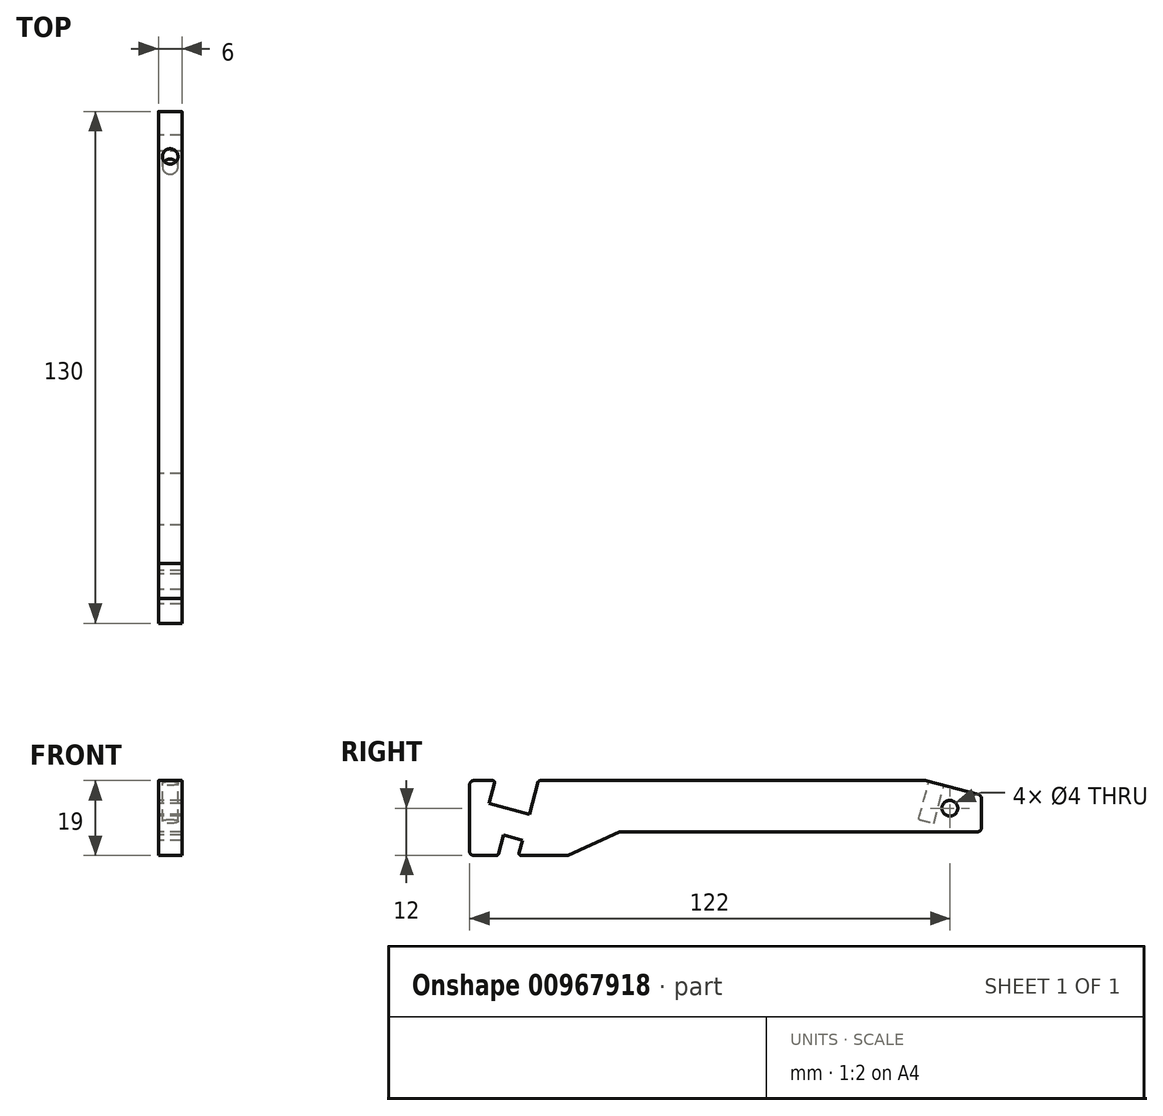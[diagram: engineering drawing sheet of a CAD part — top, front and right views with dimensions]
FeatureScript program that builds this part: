
annotation { "Feature Type Name" : "Feature", "Feature Type Description" : "" }
export const myFeature = defineFeature(function(context is Context, id is Id, definition is map)
    precondition{}
    {
        {
            var Q0;
            Q0=qCreatedBy(makeId("Right.planeOp"),FACE);
            var sketch = newSketch(context, id + "F0", { "sketchPlane" : qUnion([Q0])});
            skLineSegment(sketch, "E0.bottom", {"start": v(-1, 0) * mm, "end": v(-92, 0) * mm});
            skLineSegment(sketch, "E0.top", {"start": v(-14.13, 13) * mm, "end": v(-92, 13) * mm});
            skLineSegment(sketch, "E0.left", {"start": v(0, 1) * mm, "end": v(0, 8.48) * mm});
            skLineSegment(sketch, "E1", {"start": v(-13.87, 12.97) * mm, "end": v(-0.74, 9.45) * mm});
            skCircle(sketch, "E2", {"center": v(-8, 6) * mm, "radius": 2 * mm});
            skLineSegment(sketch, "E3.bottom", {"start": v(-105, 13) * mm, "end": v(-112.12, 13) * mm});
            skLineSegment(sketch, "E3.top", {"start": v(-105, -6) * mm, "end": v(-116.94, -6) * mm});
            skLineSegment(sketch, "E3.right", {"start": v(-130, 12) * mm, "end": v(-130, -5) * mm});
            skLineSegment(sketch, "E4", {"start": v(-92, 0) * mm, "end": v(-105, -6) * mm});
            skLineSegment(sketch, "E5", {"start": v(-92, 13) * mm, "end": v(-105, 13) * mm});
            skLineSegment(sketch, "E6", {"start": v(-112.6, 12.63) * mm, "end": v(-114.8, 4.45) * mm});
            skLineSegment(sketch, "E7", {"start": v(-116.56, -2.14) * mm, "end": v(-117.42, -5.37) * mm});
            skPoint(sketch, "E7.endSnap0", {"position": v(-117.5, -6) * mm});
            skLineSegment(sketch, "E8", {"start": v(-125.06, 7.2) * mm, "end": v(-123.67, 12.37) * mm});
            skLineSegment(sketch, "E9", {"start": v(-121.39, -0.84) * mm, "end": v(-122.67, -5.63) * mm});
            skPoint(sketch, "E10.start.orphan", {"position": v(-114.53, 5.43) * mm});
            skLineSegment(sketch, "E11", {"start": v(-125.06, 7.2) * mm, "end": v(-114.8, 4.45) * mm});
            skLineSegment(sketch, "E12", {"start": v(-121.39, -0.84) * mm, "end": v(-116.56, -2.14) * mm});
            skPoint(sketch, "E13.visualSharp", {"position": v(-130, 13) * mm});
            skArc(sketch, "E13.filletArc", {"start": v(-129, 13) * mm, "mid": v(-129.7, 12.7) * mm, "end": v(-130, 12) * mm});
            skPoint(sketch, "E14.visualSharp", {"position": v(-130, -6) * mm});
            skArc(sketch, "E14.filletArc", {"start": v(-130, -5) * mm, "mid": v(-129.7, -5.7) * mm, "end": v(-129, -6) * mm});
            skLineSegment(sketch, "E15.trimOffspring", {"start": v(-124.16, 13) * mm, "end": v(-129, 13) * mm});
            skLineSegment(sketch, "E16.trimOffspring", {"start": v(-123.15, -6) * mm, "end": v(-129, -6) * mm});
            skPoint(sketch, "E17.visualSharp", {"position": v(-123.5, 13) * mm});
            skArc(sketch, "E17.filletArc", {"start": v(-123.67, 12.37) * mm, "mid": v(-123.76, 12.8) * mm, "end": v(-124.16, 13) * mm});
            skPoint(sketch, "E18.visualSharp", {"position": v(-112.5, 13) * mm});
            skArc(sketch, "E18.filletArc", {"start": v(-112.12, 13) * mm, "mid": v(-112.42, 12.9) * mm, "end": v(-112.6, 12.63) * mm});
            skPoint(sketch, "E19.visualSharp", {"position": v(-117.6, -6) * mm});
            skArc(sketch, "E19.filletArc", {"start": v(-117.42, -5.37) * mm, "mid": v(-117.34, -5.8) * mm, "end": v(-116.94, -6) * mm});
            skPoint(sketch, "E20.visualSharp", {"position": v(-122.77, -6) * mm});
            skArc(sketch, "E20.filletArc", {"start": v(-123.15, -6) * mm, "mid": v(-122.85, -5.9) * mm, "end": v(-122.67, -5.63) * mm});
            skPoint(sketch, "E21.visualSharp", {"position": v(-14, 13) * mm});
            skArc(sketch, "E21.filletArc", {"start": v(-13.87, 12.97) * mm, "mid": v(-14, 13) * mm, "end": v(-14.13, 13) * mm});
            skPoint(sketch, "E22.visualSharp", {"position": v(0, 9.25) * mm});
            skArc(sketch, "E22.filletArc", {"start": v(0, 8.48) * mm, "mid": v(-0.2, 9.1) * mm, "end": v(-0.74, 9.45) * mm});
            skPoint(sketch, "E23.visualSharp", {"position": v(0, 0) * mm});
            skArc(sketch, "E23.filletArc", {"start": v(-1, 0) * mm, "mid": v(-0.3, 0.3) * mm, "end": v(0, 1) * mm});
            skSolve(sketch);
        }
        {
            var Q0;
            Q0 = qSketchRegion(id + "F0", true);
            extrude(context, id + "F1", {"entities" : qUnion([Q0]), "depth" : 6 * mm, "offsetDistance" : 25 * mm});
        }
        {
            var Q0;
            Q0=makeQuery(id+"F1.opExtrude","SWEPT_FACE",FACE,{"disambiguationData":[OSD([sQuery(id+"F0.wireOp",EDGE,"E1")])]});
            var sketch = newSketch(context, id + "F2", { "sketchPlane" : qUnion([Q0])});
            skCircle(sketch, "E24", {"center": v(3, -14.2) * mm, "radius": 2 * mm});
            skPoint(sketch, "E24.centerSnap0", {"position": v(3, -16.76) * mm});
            skSolve(sketch);
        }
        {
            var Q0;
            Q0=makeQuery(id+"F2.imprint","IMPRINT",FACE,{"disambiguationData":[TD([[makeQuery(id+"F2.imprint","IMPRINT",EDGE,{"derivedFrom":sQuery(id+"F2.wireOp",EDGE,"E24")}),1.0]])]});
            extrude(context, id + "F3", {"entities" : qUnion([Q0]), "operationType" : NewBodyOperationType.REMOVE, "oppositeDirection" : true, "depth" : 10 * mm, "offsetDistance" : 25 * mm});
        }
    });
